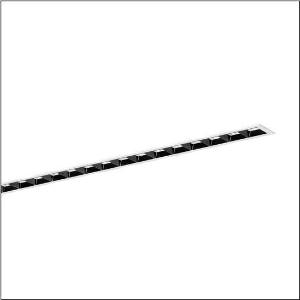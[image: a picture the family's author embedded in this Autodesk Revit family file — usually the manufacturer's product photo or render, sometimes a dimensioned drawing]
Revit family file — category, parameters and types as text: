
# Revit family: silica_r__21_51mx12tat4w_4f36
name_source: partatom
category: Lighting Fixtures
units: mm (PartAtom-declared; Revit-internal decimal feet)

## family parameters
Cut with Voids When Loaded = No
Host = Face
Light Source = No
Part Type = Normal
Room Calculation Point = No
Round Connector Dimension = Use Diameter
Shared = No

## types (1)
- --- (1 x LED, 3720 lm, 32.1 W, 6500K)
    Apparent Load = 32 VA
    CIE Flux Codes = 84 100 100 100 100
    Color Rendering = 80
    Color Temperature = 6500K
    Default Elevation = 1800 mm
    Description = Silica® 21, office luminaire, primary light control with darklight reflector, of PMMA, black, CAT 2 (L<= 3000cd/m²), light emission: direct distribution, primary light characteristic: symmetric, installation type: recessed, LED, rated luminous flux: 3.720lm, luminous efficacy: 110lm/W, light colour: 8tw, colour temperature: 2700..6500K, with terminal, 3+2-pole, max. 2.5mm², mains connection: 220..240V, AC, 50/60Hz, rated input power: 33.8W, luminaire housing, of aluminium, traffic white (RAL 9016), length: 1.228mm, width: 79mm, height: 53mm, protection rating (complete): IP20, insulation class (complete): insulation class I (protective earthing), certification: CE, permissible operating ambient temperature: 0..+35°C, standard: EN 50419, packaging unit: 1 piece
    Height = 0 mm  [stored 0 ft]
    Lamp = 1 x LED
    Lamp Light Flux = 3720 lm
    Lamp Power = 32.1 W
    Lamp count = 1
    Length = 1227 mm
    Luminous efficacy = 116 lm/W
    Manufacturer = Siteco
    ModVariant = No
    Model = 51MX12TAT4W
    Mounting Place = Ceiling
    Mounting Type = Recessed
    Number of Poles = 1
    OnlyDefault = Yes
    Power Factor = 1
    Product Name = Silica® 21
    Product group = office luminaire | ceiling recessed
    ProductGroupID = 401
    Protection Class = Protection class I
    Protection Degree = IP 20
    RLX_Detail_Level = 1
    RLX_Emergency_Light_Flux = 0 lm
    RLX_Emergency_Type = 0
    RLX_Emergency_Type_DB = No
    RlxData = <blob elided: 35609 chars, md5=1f804972>
    Socket = socket
    Standby Power = 0 W
    System Light Flux = 3720 lm
    System Power = 32 W
    Type Comments = individual setting
    Type Image = l_1297791.jpg
    URL = http://relux.com
    VarID = @adj_071503
    Voltage = 0 V
    Weight = 0.00 kg
    Width = 79 mm

note: [stored X ft] marks values corroborated as IEEE doubles in the binary element streams (Revit-internal decimal feet)

## geometry (parser evidence)
native form markers: Blend x4, Sweep x10
no freeform markers — native parametric forms only
